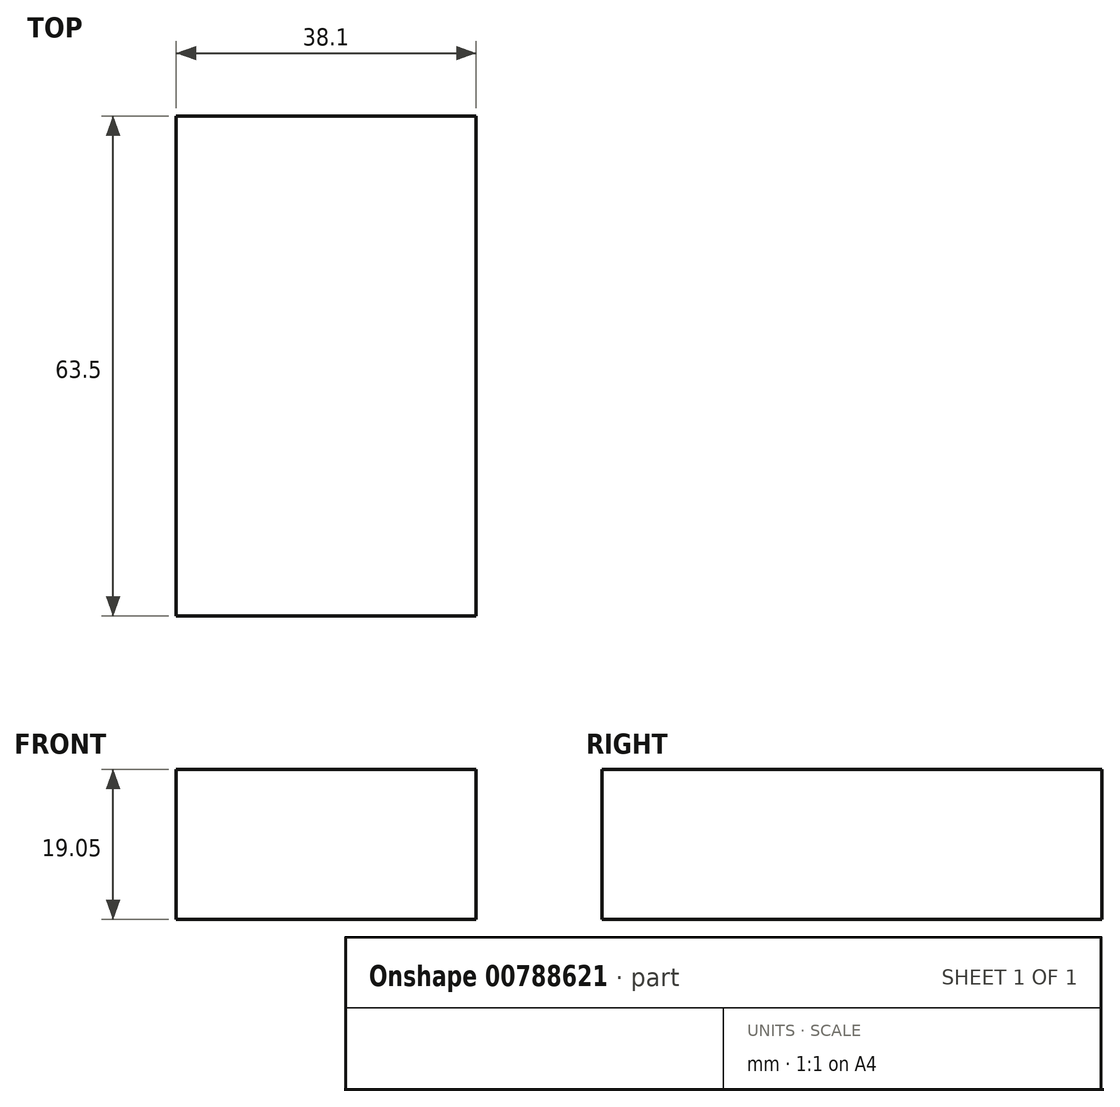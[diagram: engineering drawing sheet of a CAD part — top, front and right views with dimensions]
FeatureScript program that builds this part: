
annotation { "Feature Type Name" : "Feature", "Feature Type Description" : "" }
export const myFeature = defineFeature(function(context is Context, id is Id, definition is map)
    precondition{}
    {
        {
            var Q0;
            Q0=qCreatedBy(makeId("Top.planeOp"),FACE);
            var sketch = newSketch(context, id + "F0", { "sketchPlane" : qUnion([Q0])});
            skLineSegment(sketch, "E0.bottom", {"start": v(0, 0) * mm, "end": v(38.1, 0) * mm});
            skLineSegment(sketch, "E0.top", {"start": v(0, 63.5) * mm, "end": v(38.1, 63.5) * mm});
            skLineSegment(sketch, "E0.left", {"start": v(0, 0) * mm, "end": v(0, 63.5) * mm});
            skLineSegment(sketch, "E0.right", {"start": v(38.1, 0) * mm, "end": v(38.1, 63.5) * mm});
            skSolve(sketch);
        }
        {
            var Q0;
            Q0=qSketchRegion(id+"F0",true);
            extrude(context, id + "F1", {"entities" : qUnion([Q0]), "depth" : 19.05 * mm, "offsetDistance" : 25.4 * mm});
        }
    });
